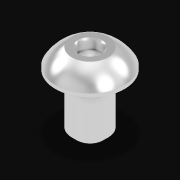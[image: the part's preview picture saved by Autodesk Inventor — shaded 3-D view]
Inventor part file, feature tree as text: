
AUTODESK INVENTOR PART (.ipt)
format: ipt  version: 2021 (Build 250183000, 183)  size: 229,376 bytes
history: native  units: in
note: dims shown in document units (in); Inventor stores cm internally (conversion verified against a paired STEP export)
features: other x32, sketch x6, extrude x1, thread x1
ambient origin geometry x8: Origin, YZ Plane, XZ Plane, XY Plane, X Axis, Y Axis, Z Axis, Center Point
bodies: Solid1 (feature_tree), Body (feature_tree)
feature tree (40):
  other  "Table"
  other  "SScrew Hex Smooth .250"
  other  "SScrew Hex Smooth .375"
  other  "SScrew Hex Smooth .500"
  other  "SScrew Hex Smooth .625"
  other  "SScrew Hex Smooth .750"
  other  "SScrew Hex Smooth .875"
  other  "SScrew Hex Smooth 1.000"
  other  "SScrew Hex Smooth 1.125"
  other  "SScrew Hex Smooth 1.250"
  other  "SScrew Hex Smooth 1.500"
  other  "SScrew Hex Smooth 1.750"
  other  "SScrew Hex Smooth 2.000"
  other  "SScrew Hex Smooth 2.250"
  other  "SScrew Hex Smooth 2.500"
  other  "SScrew Hex Threaded .250"
  other  "SScrew Hex Threaded .375"
  other  "SScrew Hex Threaded .500"
  other  "SScrew Hex Threaded .625"
  other  "SScrew Hex Threaded .750"
  other  "SScrew Hex Threaded .875"
  other  "SScrew Hex Threaded 1.000"
  other  "SScrew Hex Threaded 1.125"
  other  "SScrew Hex Threaded 1.250"
  other  "SScrew Hex Threaded 1.500"
  other  "SScrew Hex Threaded 1.750"
  other  "SScrew Hex Threaded 2.000"
  other  "SScrew Hex Threaded 2.250"
  other  "SScrew Hex Threaded 2.500"
  other  "Head"
  extrude  "Hex"  Depth=0.164in
  other  "Head Chamfer"
  thread  "Thread"  [1 undecoded]
  other  "Tapered End"
  sketch  "Sketch1"  dims[d1=0.0in d4=0.164in d5=0.156in]
  sketch  "Sketch2"  dims[d6=0.015in]
  sketch  "Sketch3"  dims[d13=0.029in]
  sketch  "Sketch4"  dims[d14=0.082in]
  sketch  "Sketch5"  dims[d15=0.087in]
  sketch  "Sketch6"  dims[d16=0.0in d17=0.047in d18=0.022in d19=0.015in d20=90.0deg d22=0.044in d23=0.0in d28=45.0deg d29=0.054in d30=90.0deg d31=30.0deg d32=60.0deg d37=0.0312in d38=0.3in d39=11.811in d40=0.0in d41=90.0deg d42=90.0deg d43=0.0in d44=0.0in d46=0.0312in d49=0.0585in d50=135.0deg d53=90.0deg d54=0.0027in d55=0.0205in d56=0.0039in]
note: 1 required parameter value undecoded (feature->parameter linkage not recoverable at this tier; creation-order binding heuristic only, values carry confidence <= 0.55)
